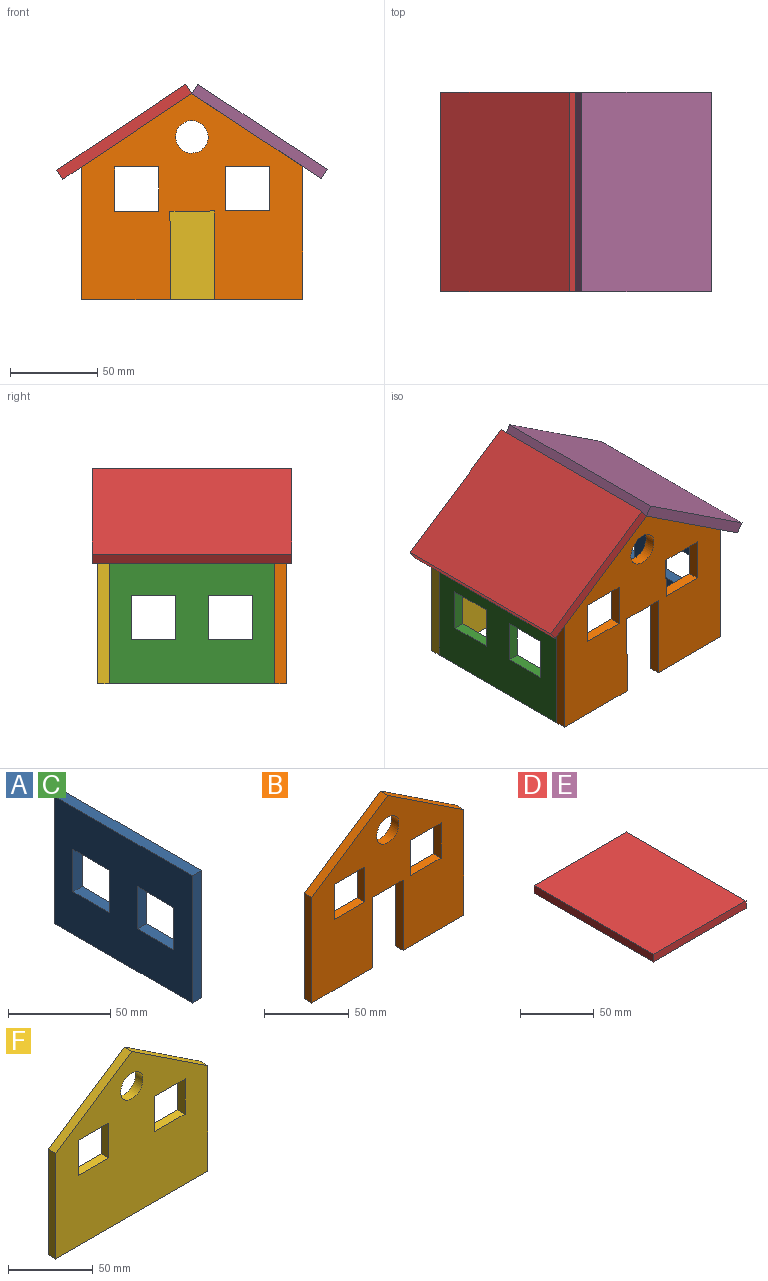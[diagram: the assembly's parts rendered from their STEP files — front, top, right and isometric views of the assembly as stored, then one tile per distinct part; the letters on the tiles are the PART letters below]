
ASSEMBLY  parts=6 mates=6
PART A: 14 faces, bbox 6.4x95.3x76.2 mm
  f0: plane 95.25x6.35mm, normal (0,0,1), area 604.8mm2, adj f1,f11,f12,f13
  f1: plane 76.2x6.35mm, normal (0,-1,0), area 483.9mm2, adj f0,f2,f12,f13
  f2: plane 95.25x6.35mm, normal (0,0,-1), area 604.8mm2, adj f1,f11,f12,f13
  f3: plane 25.4x6.35mm, normal (0,1,0), area 161.3mm2, adj f4,f9,f12,f13
  f4: plane 25.4x6.35mm, normal (0,0,-1), area 161.3mm2, adj f3,f5,f12,f13
  f5: plane 25.4x6.35mm, normal (0,-1,0), area 161.3mm2, adj f4,f9,f12,f13
  f6: plane 25.4x6.35mm, normal (0,1,0), area 161.3mm2, adj f7,f10,f12,f13
  f7: plane 25.4x6.35mm, normal (0,0,-1), area 161.3mm2, adj f6,f8,f12,f13
  f8: plane 25.4x6.35mm, normal (0,-1,0), area 161.3mm2, adj f7,f10,f12,f13
  f9: plane 25.4x6.35mm, normal (0,0,1), area 161.3mm2, adj f3,f5,f12,f13
  f10: plane 25.4x6.35mm, normal (0,0,1), area 161.3mm2, adj f6,f8,f12,f13
  f11: plane 76.2x6.35mm, normal (0,1,0), area 483.9mm2, adj f0,f2,f12,f13
  f12: plane 95.25x76.2mm, normal (1,0,0), area 5967.7mm2, adj f0,f1,f2,f3,f4,f5,f6,f7
  f13: plane 95.25x76.2mm, normal (-1,0,0), area 5967.7mm2, adj f0,f1,f2,f3,f4,f5,f6,f7
PART B: 20 faces, bbox 127x6.4x118.3 mm
  f0: plane 50.8x6.35mm, normal (-1,0,0), area 322.6mm2, adj f1,f17,f18,f19
  f1: plane 50.8x6.35mm, normal (0,0,-1), area 322.6mm2, adj f0,f2,f18,f19
  f2: plane 76.2x6.35mm, normal (1,0,0), area 483.9mm2, adj f1,f3,f18,f19
  f3: plane 63.5x42.12mm, normal (0.55,0,0.83), area 483.9mm2, adj f2,f4,f18,f19
  f4: plane 63.5x42.12mm, normal (-0.55,0,0.83), area 483.9mm2, adj f3,f5,f18,f19
  f5: plane 76.2x6.35mm, normal (-1,0,0), area 483.9mm2, adj f4,f6,f18,f19
  f6: plane 50.8x6.35mm, normal (0,0,-1), area 322.6mm2, adj f5,f7,f18,f19
  f7: plane 50.8x6.35mm, normal (1,0,0), area 322.6mm2, adj f6,f17,f18,f19
  f8: plane 25.4x6.35mm, normal (1,0,0), area 161.3mm2, adj f9,f15,f18,f19
  f9: plane 25.4x6.35mm, normal (0,0,-1), area 161.3mm2, adj f8,f10,f18,f19
  f10: plane 25.4x6.35mm, normal (-1,0,0), area 161.3mm2, adj f9,f15,f18,f19
  f11: plane 25.4x6.35mm, normal (1,0,0), area 161.3mm2, adj f12,f16,f18,f19
  f12: plane 25.4x6.35mm, normal (0,0,-1), area 161.3mm2, adj f11,f13,f18,f19
  f13: plane 25.4x6.35mm, normal (-1,0,0), area 161.3mm2, adj f12,f16,f18,f19
  f14: cylinder r=9.33mm len=18.66mm, axis (0,1,0), area 372.3mm2, adj f18,f19
  f15: plane 25.4x6.35mm, normal (0,0,1), area 161.3mm2, adj f8,f10,f18,f19
  f16: plane 25.4x6.35mm, normal (0,0,1), area 161.3mm2, adj f11,f13,f18,f19
  f17: plane 25.4x6.35mm, normal (0,0,-1), area 161.3mm2, adj f0,f7,f18,f19
  f18: plane 127x118.32mm, normal (0,-1,0), area 9497.9mm2, adj f0,f1,f2,f3,f4,f5,f6,f7
  f19: plane 127x118.32mm, normal (0,1,0), area 9497.9mm2, adj f0,f1,f2,f3,f4,f5,f6,f7
PART C: same geometry as A
PART D: 6 faces, bbox 88.9x114.3x6.4 mm
  f0: plane 114.3x6.35mm, normal (-1,0,0), area 725.8mm2, adj f1,f3,f4,f5
  f1: plane 88.9x6.35mm, normal (0,-1,0), area 564.5mm2, adj f0,f2,f4,f5
  f2: plane 114.3x6.35mm, normal (1,0,0), area 725.8mm2, adj f1,f3,f4,f5
  f3: plane 88.9x6.35mm, normal (0,1,0), area 564.5mm2, adj f0,f2,f4,f5
  f4: plane 114.3x88.9mm, normal (0,0,1), area 10161.3mm2, adj f0,f1,f2,f3
  f5: plane 114.3x88.9mm, normal (0,0,-1), area 10161.3mm2, adj f0,f1,f2,f3
PART E: same geometry as D
PART F: 16 faces, bbox 127x6.4x118.3 mm
  f0: plane 25.4x6.35mm, normal (1,0,0), area 161.3mm2, adj f1,f10,f14,f15
  f1: plane 25.4x6.35mm, normal (0,0,-1), area 161.3mm2, adj f0,f2,f14,f15
  f2: plane 25.4x6.35mm, normal (-1,0,0), area 161.3mm2, adj f1,f10,f14,f15
  f3: plane 25.4x6.35mm, normal (1,0,0), area 161.3mm2, adj f4,f11,f14,f15
  f4: plane 25.4x6.35mm, normal (0,0,-1), area 161.3mm2, adj f3,f5,f14,f15
  f5: plane 25.4x6.35mm, normal (-1,0,0), area 161.3mm2, adj f4,f11,f14,f15
  f6: plane 76.2x6.35mm, normal (-1,0,0), area 483.9mm2, adj f7,f12,f14,f15
  f7: plane 127x6.35mm, normal (0,0,-1), area 806.5mm2, adj f6,f8,f14,f15
  f8: plane 76.2x6.35mm, normal (1,0,0), area 483.9mm2, adj f7,f9,f14,f15
  f9: plane 63.5x42.12mm, normal (0.55,0,0.83), area 483.9mm2, adj f8,f12,f14,f15
  f10: plane 25.4x6.35mm, normal (0,0,1), area 161.3mm2, adj f0,f2,f14,f15
  f11: plane 25.4x6.35mm, normal (0,0,1), area 161.3mm2, adj f3,f5,f14,f15
  f12: plane 63.5x42.12mm, normal (-0.55,0,0.83), area 483.9mm2, adj f6,f9,f14,f15
  f13: cylinder r=9.33mm len=18.66mm, axis (0,1,0), area 372.3mm2, adj f14,f15
  f14: plane 127x118.32mm, normal (0,-1,0), area 10788.2mm2, adj f0,f1,f2,f3,f4,f5,f6,f7
  f15: plane 127x118.32mm, normal (0,1,0), area 10788.2mm2, adj f0,f1,f2,f3,f4,f5,f6,f7
PLACE A rot(axis=(0,-1,0),0.1deg) t=(-11.19,130.63,68.67)mm
PLACE B rot(axis=(0,-1,0),0.1deg) t=(-68.47,83,87.54)mm
PLACE C rot(axis=(0,-1,0),0.1deg) t=(-131.84,130.63,68.37)mm
PLACE D rot(axis=(0,-1,0),33.7deg) t=(-105.52,130.63,124.09)mm
PLACE E rot(axis=(0,1,0),33.4deg) t=(-31.44,130.63,124.27)mm
PLACE F rot(axis=(0,-1,0),0.1deg) t=(-68.39,184.6,87.71)mm
MATE fastened C.f11 <-> F.f14  axis (0,1,0) through (-131.93,178.25,106.47)mm
MATE fastened B.f19 <-> A.f1  axis (0,1,0) through (-4.93,83,106.79)mm
MATE fastened D.f5 <-> F.f12  axis (0.55,0,-0.83) through (-68.54,187.78,148.75)mm
MATE fastened F.f14 <-> A.f11  axis (0,-1,0) through (-4.93,178.25,106.79)mm
MATE fastened C.f1 <-> B.f19  axis (0,-1,0) through (-131.93,83,106.47)mm
MATE fastened E.f5 <-> B.f3  axis (-0.55,0,-0.83) through (-68.54,73.48,148.75)mm
